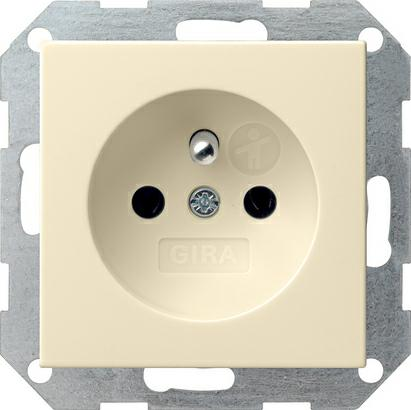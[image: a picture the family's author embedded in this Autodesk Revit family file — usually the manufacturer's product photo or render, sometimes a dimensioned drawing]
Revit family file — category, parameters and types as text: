
# Revit family: E_Cable Junction Box_MEPcontent_Spelsberg_BS 1_INT-EN
name_source: partatom
category: Electrical Fixtures
revit_build: Autodesk Revit 2017 (Build: 20160225_1515(x64)
units: mm (PartAtom-declared; Revit-internal decimal feet)

## family parameters
Always vertical = Yes
Cut with Voids When Loaded = No
Maintain Annotation Orientation = Yes
OmniClass Number = 23.80.30.14.24
OmniClass Title = Junction Boxes
Part Type = Junction Box
Room Calculation Point = No
Round Connector Dimension = Use Diameter
Shared = No
Work Plane-Based = No

## types (1)
- BS 1
    3D Representation = 3DGeometry
    Article Description = Equipment installation box BS 1
    Article Type = BS 1
    Blue = Color RAL 5013
    Description = Equipment installation box BS 1
    ETIM Article Class = EC002601
    Green = Color RAL 6018
    Height = 59.1 mm  [stored 0.193898 ft]
    IFCExportAs = IfcJunctionBox
    IFCExportType = NOTDEFINED
    Length = 86 mm  [stored 0.282152 ft]
    Manufacturer = Spelsberg
    Manufacturer Art. No. = 97400101
    Manufacturer URL = http://www.spelsberg.com
    Model = BS 1
    Placeholder Height = 59.1 mm  [stored 0.193898 ft]
    Product Line = Spelsberg
    Revit Version = 2017
    Rotation U-Axis Correction = 0.00°
    Rotation U-Axis Default Correction = 0.00°
    Rotation V-Axis Correction = 0.00°
    Rotation V-Axis Default Correction = 0.00°
    Rotation W-Axis Correction = 0.00°
    Rotation W-Axis Default Correction = 0.00°
    Voltage = 230 V
    Width = 86 mm  [stored 0.282152 ft]

note: [stored X ft] marks values corroborated as IEEE doubles in the binary element streams (Revit-internal decimal feet)

## geometry (parser evidence)
native form markers: Sweep x18
no freeform markers — native parametric forms only
